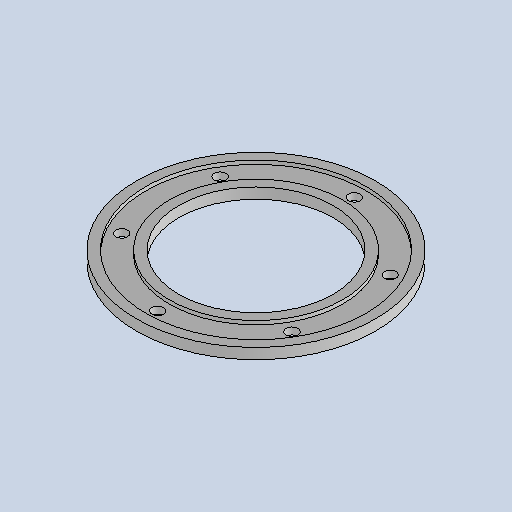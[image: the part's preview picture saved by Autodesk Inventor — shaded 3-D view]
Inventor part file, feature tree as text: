
AUTODESK INVENTOR PART (.ipt)
format: ipt  version: 2025 (Build 290162010, 162A)  size: 331,264 bytes
history: native  units: mm
features: sketch x3, extrude x2, other x2, sheet_metal_op x1, pattern_circular x1
ambient origin geometry x8: Origin, YZ Plane, XZ Plane, XY Plane, X Axis, Y Axis, Z Axis, Center Point
bodies: Body1 (feature_tree)
feature tree (9):
  sheet_metal_op  "Face1"
  extrude  "Extrusion5"  Depth=10.0mm
  extrude  "Extrusion6"  Depth=3.5mm TaperAngle=0.0deg
  pattern_circular  "Circular Pattern3"  [2 undecoded]
  sketch  "Sketch6"  dims[d45=10.0mm d46=145.0mm]
  other  "Plate1"
  sketch  "Sketch7"  dims[d47=225.0mm d48=3.5mm d49=0.0mm]
  sketch  "Sketch8"  dims[d50=11.0mm d51=185.0mm d52=3.5mm d53=0.0mm d54=60.0mm d55=360.0deg d57=163.0mm d58=207.0mm]
  other  "Definition1"
note: 2 required parameter values undecoded (feature->parameter linkage not recoverable at this tier; creation-order binding heuristic only, values carry confidence <= 0.55)
